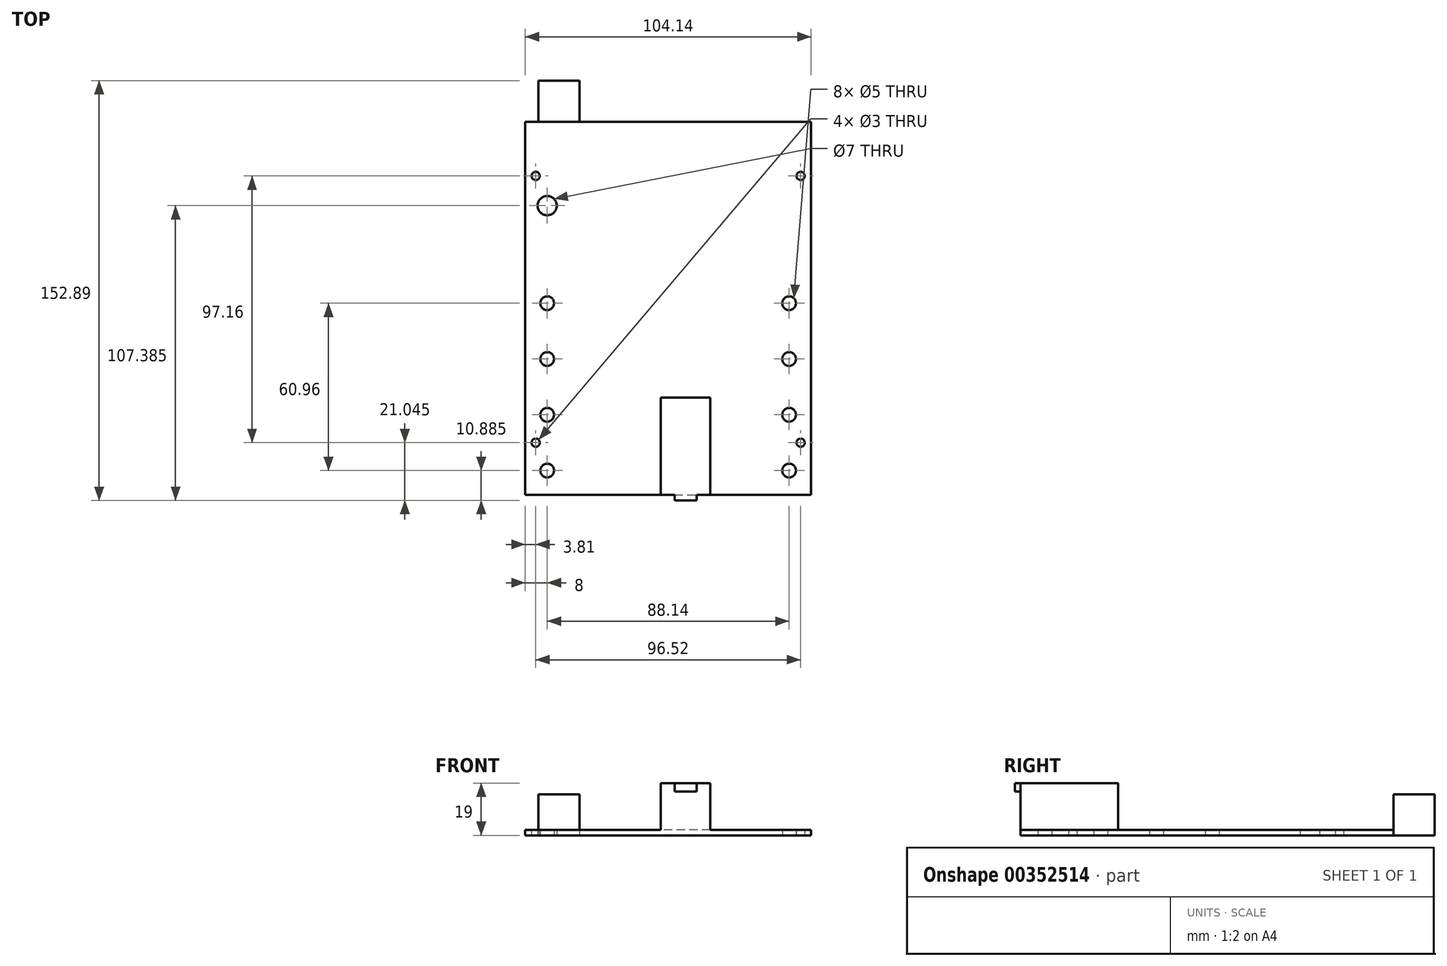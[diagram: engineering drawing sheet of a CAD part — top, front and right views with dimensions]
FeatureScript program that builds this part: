
annotation { "Feature Type Name" : "Feature", "Feature Type Description" : "" }
export const myFeature = defineFeature(function(context is Context, id is Id, definition is map)
    precondition{}
    {
        {
            var Q0;
            Q0=qCreatedBy(makeId("Top.planeOp"),FACE);
            var sketch = newSketch(context, id + "F0", { "sketchPlane" : qUnion([Q0])});
            skLineSegment(sketch, "E0.bottom", {"start": v(52.07, -67.94) * mm, "end": v(-52.07, -67.94) * mm});
            skLineSegment(sketch, "E0.top", {"start": v(52.07, 67.95) * mm, "end": v(-52.07, 67.95) * mm});
            skLineSegment(sketch, "E0.left", {"start": v(52.07, -67.94) * mm, "end": v(52.07, 67.95) * mm});
            skLineSegment(sketch, "E0.right", {"start": v(-52.07, -67.94) * mm, "end": v(-52.07, 67.95) * mm});
            skPoint(sketch, "E0.middle", {"position": v(0, 0) * mm});
            skCircle(sketch, "E1", {"center": v(-48.26, 48.27) * mm, "radius": 1.5 * mm});
            skCircle(sketch, "E2", {"center": v(48.26, -48.9) * mm, "radius": 1.5 * mm});
            skCircle(sketch, "E3", {"center": v(48.26, 48.27) * mm, "radius": 1.5 * mm});
            skCircle(sketch, "E4", {"center": v(-48.26, -48.9) * mm, "radius": 1.5 * mm});
            skCircle(sketch, "E5", {"center": v(-44.07, -59.05) * mm, "radius": 2.5 * mm});
            skCircle(sketch, "E6", {"center": v(-44.07, -38.73) * mm, "radius": 2.5 * mm});
            skCircle(sketch, "E7", {"center": v(-44.07, -18.41) * mm, "radius": 2.5 * mm});
            skCircle(sketch, "E8", {"center": v(-44.07, 1.9) * mm, "radius": 2.5 * mm});
            skCircle(sketch, "E9", {"center": v(-44.07, 37.45) * mm, "radius": 3.5 * mm});
            skCircle(sketch, "E10", {"center": v(44.07, -59.05) * mm, "radius": 2.5 * mm});
            skCircle(sketch, "E11", {"center": v(44.07, -38.73) * mm, "radius": 2.5 * mm});
            skCircle(sketch, "E12", {"center": v(44.07, -18.41) * mm, "radius": 2.5 * mm});
            skCircle(sketch, "E13", {"center": v(44.07, 1.9) * mm, "radius": 2.5 * mm});
            skSolve(sketch);
        }
        {
            var Q0;
            Q0=qSketchRegion(id+"F0",true);
            extrude(context, id + "F1", {"entities" : qUnion([Q0]), "depth" : 2 * mm});
        }
        {
            var Q0;
            Q0=makeQuery(id+"F1.opExtrude","CAP_FACE",FACE,{"disambiguationData":[OSD([sQuery(id+"F0.wireOp",EDGE,"E0.bottom"),sQuery(id+"F0.wireOp",EDGE,"E0.top"),sQuery(id+"F0.wireOp",EDGE,"E0.left"),sQuery(id+"F0.wireOp",EDGE,"E0.right"),sQuery(id+"F0.wireOp",EDGE,"E1"),sQuery(id+"F0.wireOp",EDGE,"E2"),sQuery(id+"F0.wireOp",EDGE,"E3"),sQuery(id+"F0.wireOp",EDGE,"E4")])],"isStart":false});
            cPlane(context, id + "F2", {"entities" : qUnion([Q0]), "cplaneType" : CPlaneType.OFFSET, "offset" : 0 * mm, "width" : 150 * mm, "height" : 150 * mm});
        }
        {
            var Q0;
            Q0=qCreatedBy(id+"F2.planeOp",FACE);
            var sketch = newSketch(context, id + "F3", { "sketchPlane" : qUnion([Q0])});
            skLineSegment(sketch, "E14.0", {"start": v(-52.07, -67.94) * mm, "end": v(-52.07, 67.95) * mm, "construction": true});
            skLineSegment(sketch, "E15.0", {"start": v(52.07, 67.95) * mm, "end": v(-52.07, 67.95) * mm, "construction": true});
            skLineSegment(sketch, "E16.0", {"start": v(52.07, -67.94) * mm, "end": v(52.07, 67.95) * mm, "construction": true});
            skLineSegment(sketch, "E17.0", {"start": v(52.07, -67.94) * mm, "end": v(-52.07, -67.94) * mm, "construction": true});
            skLineSegment(sketch, "E18.bottom", {"start": v(-47.24, 67.95) * mm, "end": v(-32.24, 67.95) * mm});
            skLineSegment(sketch, "E18.top", {"start": v(-47.24, 82.95) * mm, "end": v(-32.24, 82.95) * mm});
            skLineSegment(sketch, "E18.left", {"start": v(-47.24, 67.95) * mm, "end": v(-47.24, 82.95) * mm});
            skLineSegment(sketch, "E18.right", {"start": v(-32.24, 67.95) * mm, "end": v(-32.24, 82.95) * mm});
            skSolve(sketch);
        }
        {
            var Q0;
            Q0=qSketchRegion(id+"F3",true);
            extrude(context, id + "F4", {"entities" : qUnion([Q0]), "operationType" : NewBodyOperationType.ADD, "depth" : 13 * mm, "hasSecondDirection" : true, "secondDirectionOppositeDirection" : true, "secondDirectionDepth" : 2 * mm});
        }
        {
            var Q0;
            Q0=qCreatedBy(id+"F2.planeOp",FACE);
            var sketch = newSketch(context, id + "F5", { "sketchPlane" : qUnion([Q0])});
            skLineSegment(sketch, "E19.0", {"start": v(52.07, -67.94) * mm, "end": v(-52.07, -67.94) * mm, "construction": true});
            skLineSegment(sketch, "E20.0", {"start": v(-52.07, -67.94) * mm, "end": v(-52.07, 67.95) * mm, "construction": true});
            skLineSegment(sketch, "E21.0", {"start": v(52.07, -67.94) * mm, "end": v(52.07, 67.95) * mm, "construction": true});
            skLineSegment(sketch, "E22.bottom", {"start": v(15.35, -67.94) * mm, "end": v(-2.65, -67.94) * mm});
            skLineSegment(sketch, "E22.top", {"start": v(15.35, -32.44) * mm, "end": v(-2.65, -32.44) * mm});
            skLineSegment(sketch, "E22.left", {"start": v(15.35, -67.94) * mm, "end": v(15.35, -32.44) * mm});
            skLineSegment(sketch, "E22.right", {"start": v(-2.65, -67.94) * mm, "end": v(-2.65, -32.44) * mm});
            skLineSegment(sketch, "E23", {"start": v(6.35, 0) * mm, "end": v(6.35, -67.94) * mm, "construction": true});
            skSolve(sketch);
        }
        {
            var Q0;
            Q0=qSketchRegion(id+"F5",true);
            extrude(context, id + "F6", {"entities" : qUnion([Q0]), "operationType" : NewBodyOperationType.ADD, "depth" : 17 * mm});
        }
        {
            var Q0;
            Q0=makeQuery(id+"F6.boolean.opBoolean","MERGE",FACE,{"derivedFrom":[makeQuery(id+"F1.opExtrude","SWEPT_FACE",FACE,{"disambiguationData":[OSD([sQuery(id+"F0.wireOp",EDGE,"E0.bottom")])]}),makeQuery(id+"F6.opExtrude","SWEPT_FACE",FACE,{"disambiguationData":[OSD([sQuery(id+"F5.wireOp",EDGE,"E22.bottom")])]})]});
            cPlane(context, id + "F7", {"entities" : qUnion([Q0]), "cplaneType" : CPlaneType.OFFSET, "offset" : 0 * mm, "width" : 150 * mm, "height" : 150 * mm});
        }
        {
            var Q0;
            Q0=qCreatedBy(id+"F7.planeOp",FACE);
            var sketch = newSketch(context, id + "F8", { "sketchPlane" : qUnion([Q0])});
            skLineSegment(sketch, "E24.0", {"start": v(15.35, 19) * mm, "end": v(-2.65, 19) * mm, "construction": true});
            skLineSegment(sketch, "E25.0", {"start": v(52.07, 0) * mm, "end": v(-52.07, 0) * mm, "construction": true});
            skLineSegment(sketch, "E26.bottom", {"start": v(2.35, 19) * mm, "end": v(10.35, 19) * mm});
            skLineSegment(sketch, "E26.top", {"start": v(2.35, 16) * mm, "end": v(10.35, 16) * mm});
            skLineSegment(sketch, "E26.left", {"start": v(2.35, 19) * mm, "end": v(2.35, 16) * mm});
            skLineSegment(sketch, "E26.right", {"start": v(10.35, 19) * mm, "end": v(10.35, 16) * mm});
            skLineSegment(sketch, "E27", {"start": v(6.35, 19) * mm, "end": v(6.35, 5.81) * mm, "construction": true});
            skPoint(sketch, "E27.endSnap0", {"position": v(6.35, 19) * mm});
            skSolve(sketch);
        }
        {
            var Q0;
            Q0=qSketchRegion(id+"F8",true);
            extrude(context, id + "F9", {"entities" : qUnion([Q0]), "operationType" : NewBodyOperationType.ADD, "depth" : 2 * mm});
        }
    });
